# Revit family: Air-Curtain_Climate-Control_PoweredAire_TIG-2Heater
name_source: partatom
category: Mechanical Equipment
revit_build: Autodesk Revit 2016 (Build: 20150714_1515(x64)
units: mm (PartAtom-declared; Revit-internal decimal feet)

## family parameters
Cut with Voids When Loaded = No
Host = Face
OmniClass Number = 23.75.35.17.21
OmniClass Title = Air Curtains
Part Type = Normal
Room Calculation Point = No
Round Connector Dimension = Use Diameter
Shared = No

## types (3) — shared parameters
Assembly Code = D3090400
Construction Details = http://www.arcat.com
Default Elevation = 0' - 0"
Exhaust Connection Diameter = 0' - 5"
Green Building-LEED = http://www.arcat.com
HVAC_Primary CFM = 0 CFM
Heater Hanging Width = 2' - 6 5/8"
Heating Element Load = 0 W
Keynote = 23 34 33
Manufacturer = Powered Aire, Inc
Manufacturer Fax = 724-588-3371
Manufacturer Website = http://www.poweredaire.com
Max Height = 12' - 0"
Motor HP = 0.75
Motor RPM = 1630
Overall Depth = 6' - 0 3/4"
Power Rating = 0 W
Product Data = http://www.arcat.com
Revision = R1_2016-08
Sales Information = http://www.poweredaire.com
Sound Pressure = >63 dBA
Specification = http://www.arcat.com
Standards Conformance = ETL  ;  Made in USA
URL = http://www.poweredaire.com
Unit Depth = 1' - 8 1/4"
Unit Height = 1' - 4 3/4"
Unit Width Notes = Other Widths available.
zero-valued in all types: Expected Lifespan (Years), Heater Weight, Maintenance Schedule (Months), Warranty Duration (Years)

## per-type parameters (varying)
| type | Description | HVAC_BTU Input | HVAC_BTU Output | HVAC_Outlet Velocity | HVAC_Outlet Velocity Uniformity | HVAC_Outlet Volume | HVAC_Temperature Rise | Model | Motor Count | Mounting Width | Nozzle Width | Unit Weight | Unit Width |
| 144'' Nozzle | Powered Aire Indirect Gas Heated Climate Control Air Curtain - TIG-4-144 as Specified | 250000.0 Btu/h | 400000.0 Btu/h | 3700 FPM | 0.95 | 10200 CFM | 36 °F | TIG-4-144 | 4 | 12' - 1 23/32" | 12' - 0 7/32" | 1000 | 12' - 3 7/32" |
| 132'' Nozzle | Powered Aire Indirect Gas Heated Climate Control Air Curtain - TIG-3-132 as Specified | 200000.0 Btu/h | 320000.0 Btu/h | 2800 FPM | 0.94 | 7600 CFM | 39 °F | TIG-3-132 | 3 | 11' - 1 21/32" | 11' - 0 5/32" | 830 | 11' - 3 5/32" |
| 120'' Nozzle | Powered Aire Indirect Gas Heated Climate Control Air Curtain - TIG-3-120 as Specified | 200000.0 Btu/h | 320000.0 Btu/h | 3200 FPM | 0.95 | 7600 CFM | 39 °F | TIG-3-120 | 3 | 10' - 1 21/32" | 10' - 0 5/32" | 680 | 10' - 3 5/32" |

## geometry (parser evidence)
native form markers: Sweep x8
no freeform markers — native parametric forms only
